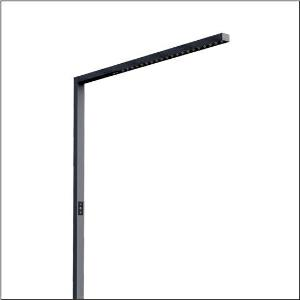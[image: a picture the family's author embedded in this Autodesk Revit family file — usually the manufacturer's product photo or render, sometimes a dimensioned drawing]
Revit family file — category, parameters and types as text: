
# Revit family: silica_r__31_floor_51my52fa4cb_29ea
name_source: partatom
category: Lighting Fixtures
units: mm (PartAtom-declared; Revit-internal decimal feet)

## family parameters
Cut with Voids When Loaded = No
Host = Face
Light Source = No
Part Type = Normal
Room Calculation Point = No
Round Connector Dimension = Use Diameter
Shared = No

## types (1)
- Silica® 31 Floor (1 x LED, 10600 lm, 75 W, 4000K)
    Apparent Load = 75 VA
    CIE Flux Codes = 86 100 100 24 100
    Color Rendering = 80
    Color Temperature = 4000K
    Default Elevation = 1800 mm
    Description = Silica® 31 Floor, floorstanding luminaire, secondary optical cover: cover panel, of PMMA, light emission: direct/indirect distribution, primary light characteristic: symmetric, installation type: not mounted, LED, rated luminous flux: 10.600lm, luminous efficacy: 141lm/W, light colour: 840, colour temperature: 4000K, daylight-dependent control, with cable with plug, mains connection: 230V, AC, 50Hz, connection cable pre-assembled, rated input power: 75W, luminaire head, of aluminium, jet black (RAL 9005), length: 1.203mm, width: 52mm, supporting column, angular, of aluminium, jet black (RAL 9005), baseplate, of steel, jet black (RAL 9005), protection rating (complete): IP20, insulation class (complete): insulation class I (protective earthing), certification: CE, permissible operating ambient temperature: -20..+40°C, standard: EN 50419, packaging unit: 1 piece
    Height = 36 mm
    Lamp = 1 x LED
    Lamp Light Flux = 10600 lm
    Lamp Power = 75 W
    Lamp count = 1
    Length = 1203 mm
    Luminous efficacy = 141 lm/W
    Manufacturer = Siteco
    ModVariant = No
    Model = 51MY52FA4CB
    Mounting Place = Floor
    Mounting Type = Freestanding
    Number of Poles = 1
    OnlyDefault = Yes
    Power Factor = 1
    Product Name = Silica® 31 Floor
    Product group = floorstanding luminaire
    ProductGroupID = 1301
    Protection Class = Protection class I
    Protection Degree = IP 20
    RLX_Detail_Level = 1
    RLX_Emergency_Light_Flux = 0 lm
    RLX_Emergency_Type = 0
    RLX_Emergency_Type_DB = No
    RlxData = <blob elided: 20097 chars, md5=d7d352b8>
    Socket = socket
    Standby Power = 0 W
    System Light Flux = 10600 lm
    System Power = 75 W
    Type Comments = Product without accessories
    Type Image = l_1275297.jpg
    URL = http://relux.com
    VarID = ---
    Voltage = 0 V
    Weight = 0.00 kg
    Width = 52 mm  [stored 0.170604 ft]

note: [stored X ft] marks values corroborated as IEEE doubles in the binary element streams (Revit-internal decimal feet)

## geometry (parser evidence)
native form markers: Blend x4, Sweep x13
no freeform markers — native parametric forms only
